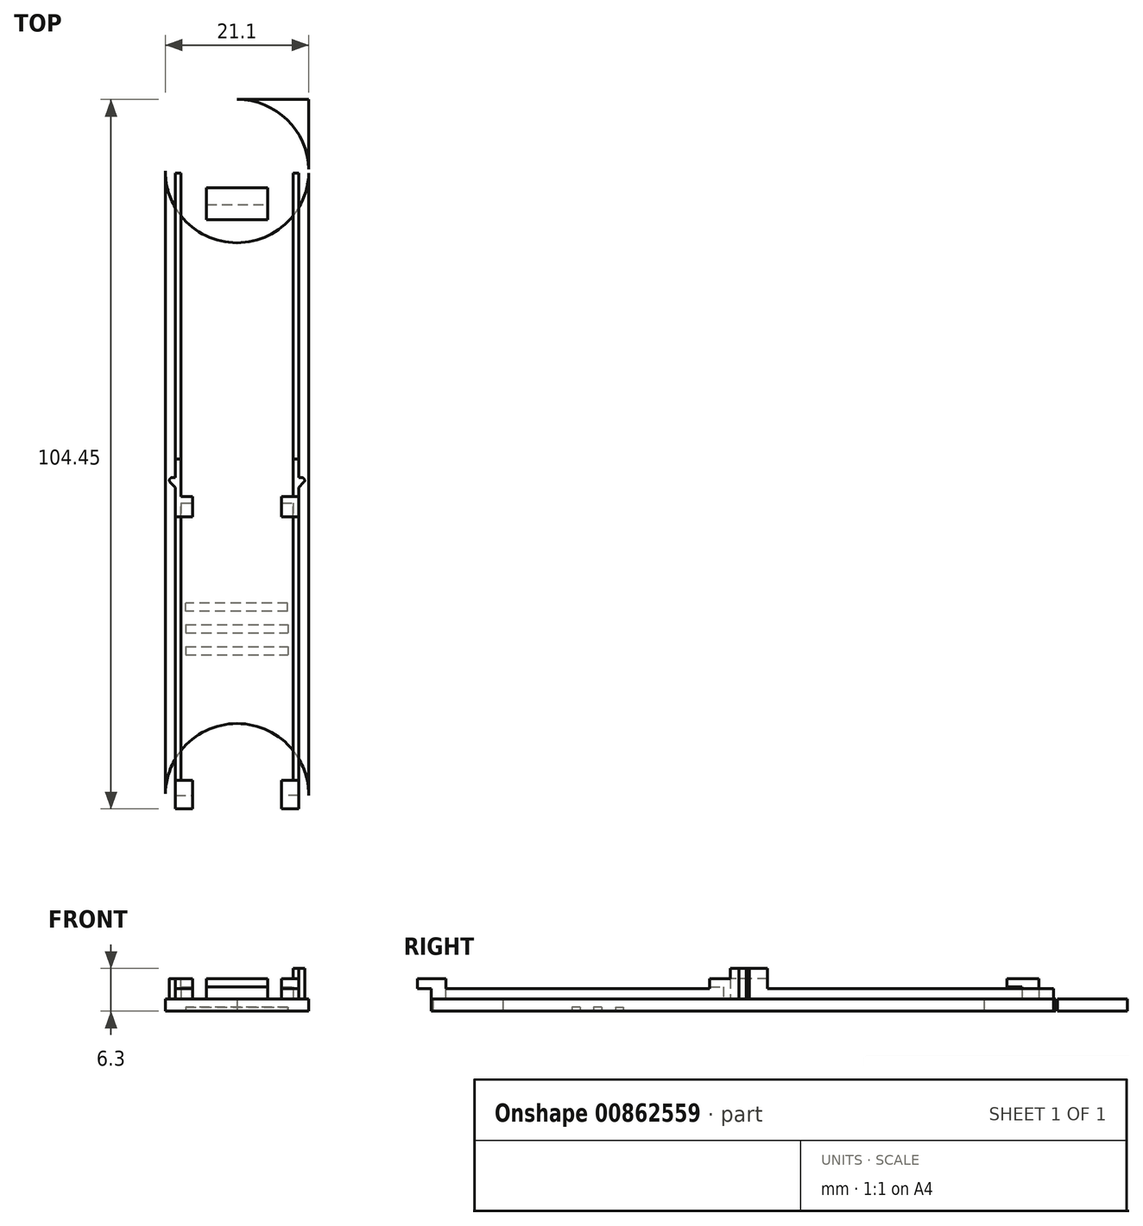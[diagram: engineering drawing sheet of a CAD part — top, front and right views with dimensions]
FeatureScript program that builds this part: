
annotation { "Feature Type Name" : "Feature", "Feature Type Description" : "" }
export const myFeature = defineFeature(function(context is Context, id is Id, definition is map)
    precondition{}
    {
        {
            var Q0;
            Q0=qCreatedBy(makeId("Top.planeOp"),FACE);
            var sketch = newSketch(context, id + "F0", { "sketchPlane" : qUnion([Q0])});
            skLineSegment(sketch, "E0.bottom", {"start": v(10.55, -56.5) * mm, "end": v(-10.55, -56.5) * mm});
            skLineSegment(sketch, "E0.top", {"start": v(10.55, 56.5) * mm, "end": v(-10.55, 56.5) * mm});
            skLineSegment(sketch, "E0.left", {"start": v(10.55, -56.5) * mm, "end": v(10.55, 56.5) * mm});
            skLineSegment(sketch, "E0.right", {"start": v(-10.55, -56.5) * mm, "end": v(-10.55, 56.5) * mm});
            skPoint(sketch, "E0.middle", {"position": v(0, 0) * mm});
            skCircle(sketch, "E1", {"center": v(0, 45.95) * mm, "radius": 10.55 * mm});
            skPoint(sketch, "E1.first.point", {"position": v(-10.55, 45.95) * mm});
            skPoint(sketch, "E1.second.point", {"position": v(0, 56.5) * mm});
            skPoint(sketch, "E1.third.point", {"position": v(10.55, 45.66) * mm});
            skCircle(sketch, "E2", {"center": v(0, -45.95) * mm, "radius": 10.55 * mm});
            skPoint(sketch, "E2.first.point", {"position": v(0, -35.4) * mm});
            skPoint(sketch, "E2.second.point", {"position": v(0, -56.5) * mm});
            skPoint(sketch, "E2.third.point", {"position": v(-10.55, -46.2) * mm});
            skSolve(sketch);
        }
        {
            var Q0;
            {var subQ0=sQuery(id+"F0.wireOp",EDGE,"E1");var subQ1=sQuery(id+"F0.wireOp",EDGE,"E0.left");var subQ2=makeQuery(id+"F0.imprint","INTERSECT",VERTEX,{"disambiguationData":[OD(0.0)],"derivedFrom":[subQ1,subQ0]});Q0=makeQuery(id+"F0.imprint","IMPRINT",FACE,{"disambiguationData":[TD([[makeQuery(id+"F0.imprint","IMPRINT",EDGE,{"disambiguationData":[TD([[subQ2,-1.0]])],"derivedFrom":subQ1}),-1.0]])]});}
            var Q1;
            {var subQ0=sQuery(id+"F0.wireOp",EDGE,"E2");var subQ1=sQuery(id+"F0.wireOp",EDGE,"E0.right");var subQ2=makeQuery(id+"F0.imprint","INTERSECT",VERTEX,{"disambiguationData":[OD(0.0)],"derivedFrom":[subQ1,subQ0]});Q1=makeQuery(id+"F0.imprint","IMPRINT",FACE,{"disambiguationData":[TD([[makeQuery(id+"F0.imprint","IMPRINT",EDGE,{"disambiguationData":[TD([[subQ2,-1.0]])],"derivedFrom":subQ1}),1.0]])]});}
            var Q2;
            {var subQ0=sQuery(id+"F0.wireOp",EDGE,"E2");var subQ1=sQuery(id+"F0.wireOp",EDGE,"E0.left");var subQ2=makeQuery(id+"F0.imprint","INTERSECT",VERTEX,{"derivedFrom":[subQ1,subQ0]});Q2=makeQuery(id+"F0.imprint","IMPRINT",FACE,{"disambiguationData":[TD([[makeQuery(id+"F0.imprint","IMPRINT",EDGE,{"disambiguationData":[TD([[subQ2,-1.0]])],"derivedFrom":subQ1}),1.0]])]});}
            var Q3;
            {var subQ0=sQuery(id+"F0.wireOp",EDGE,"E2");var subQ1=sQuery(id+"F0.wireOp",EDGE,"E0.right");var subQ2=makeQuery(id+"F0.imprint","INTERSECT",VERTEX,{"disambiguationData":[OD(0.0)],"derivedFrom":[subQ1,subQ0]});Q3=makeQuery(id+"F0.imprint","IMPRINT",FACE,{"disambiguationData":[TD([[makeQuery(id+"F0.imprint","IMPRINT",EDGE,{"disambiguationData":[TD([[subQ2,-1.0]])],"derivedFrom":subQ1}),-1.0]])]});}
            var Q4;
            {var subQ0=sQuery(id+"F0.wireOp",EDGE,"E1");var subQ1=sQuery(id+"F0.wireOp",EDGE,"E0.left");var subQ2=makeQuery(id+"F0.imprint","INTERSECT",VERTEX,{"disambiguationData":[OD(0.0)],"derivedFrom":[subQ1,subQ0]});Q4=makeQuery(id+"F0.imprint","IMPRINT",FACE,{"disambiguationData":[TD([[makeQuery(id+"F0.imprint","IMPRINT",EDGE,{"disambiguationData":[TD([[subQ2,-1.0]])],"derivedFrom":subQ1}),1.0]])]});}
            extrude(context, id + "F1", {"entities" : qUnion([Q0, Q1, Q2, Q3, Q4]), "depth" : 1.8 * mm, "offsetDistance" : 25.4 * mm});
        }
        {
            var Q0;
            Q0=makeQuery(id+"F1.opExtrude","CAP_FACE",FACE,{"disambiguationData":[OSD([sQuery(id+"F0.wireOp",EDGE,"E0.left"),sQuery(id+"F0.wireOp",EDGE,"E0.right"),sQuery(id+"F0.wireOp",EDGE,"E1"),sQuery(id+"F0.wireOp",EDGE,"E2")])],"isStart":true});
            var sketch = newSketch(context, id + "F2", { "sketchPlane" : qUnion([Q0])});
            skLineSegment(sketch, "E3", {"start": v(0, -45.95) * mm, "end": v(0, -45.95) * mm});
            skLineSegment(sketch, "E4", {"start": v(0, -45.95) * mm, "end": v(-2.54, -45.95) * mm});
            skLineSegment(sketch, "E5", {"start": v(-2.54, -45.95) * mm, "end": v(0, -50.24) * mm});
            skLineSegment(sketch, "E6", {"start": v(0, -50.24) * mm, "end": v(2.66, -45.95) * mm});
            skLineSegment(sketch, "E7", {"start": v(2.66, -45.95) * mm, "end": v(0, -45.95) * mm});
            skLineSegment(sketch, "E8.bottom", {"start": v(7.45, 18.85) * mm, "end": v(-7.55, 18.85) * mm});
            skLineSegment(sketch, "E8.top", {"start": v(7.45, 17.65) * mm, "end": v(-7.55, 17.65) * mm});
            skLineSegment(sketch, "E8.left", {"start": v(7.45, 18.85) * mm, "end": v(7.45, 17.65) * mm});
            skLineSegment(sketch, "E8.right", {"start": v(-7.55, 18.85) * mm, "end": v(-7.55, 17.65) * mm});
            skLineSegment(sketch, "E9.bottom", {"start": v(-7.55, 20.85) * mm, "end": v(7.46, 20.85) * mm});
            skLineSegment(sketch, "E9.left", {"start": v(-7.55, 20.85) * mm, "end": v(-7.55, 22.05) * mm});
            skLineSegment(sketch, "E9.right", {"start": v(7.46, 20.85) * mm, "end": v(7.46, 22.05) * mm});
            skLineSegment(sketch, "E10", {"start": v(-7.55, 22.05) * mm, "end": v(7.46, 22.05) * mm});
            skLineSegment(sketch, "E11.bottom", {"start": v(-7.55, 24.05) * mm, "end": v(7.46, 24.05) * mm});
            skLineSegment(sketch, "E11.top", {"start": v(-7.55, 25.25) * mm, "end": v(7.46, 25.25) * mm});
            skLineSegment(sketch, "E11.left", {"start": v(-7.55, 24.05) * mm, "end": v(-7.55, 25.25) * mm});
            skLineSegment(sketch, "E11.right", {"start": v(7.46, 24.05) * mm, "end": v(7.46, 25.25) * mm});
            skLineSegment(sketch, "E12", {"start": v(10.55, 0) * mm, "end": v(-10.55, -0.12) * mm, "construction": true});
            skSolve(sketch);
        }
        {
            var Q0;
            Q0=makeQuery(id+"F2.imprint","IMPRINT",FACE,{"disambiguationData":[TD([[makeQuery(id+"F2.imprint","IMPRINT",EDGE,{"derivedFrom":sQuery(id+"F2.wireOp",EDGE,"E4")}),1.0]])]});
            var Q1;
            Q1=makeQuery(id+"F2.imprint","IMPRINT",FACE,{"disambiguationData":[TD([[makeQuery(id+"F2.imprint","IMPRINT",EDGE,{"derivedFrom":sQuery(id+"F2.wireOp",EDGE,"E8.bottom")}),1.0]])]});
            var Q2;
            Q2=makeQuery(id+"F2.imprint","IMPRINT",FACE,{"disambiguationData":[TD([[makeQuery(id+"F2.imprint","IMPRINT",EDGE,{"derivedFrom":sQuery(id+"F2.wireOp",EDGE,"E9.bottom")}),1.0]])]});
            var Q3;
            Q3=makeQuery(id+"F2.imprint","IMPRINT",FACE,{"disambiguationData":[TD([[makeQuery(id+"F2.imprint","IMPRINT",EDGE,{"derivedFrom":sQuery(id+"F2.wireOp",EDGE,"E11.bottom")}),1.0]])]});
            extrude(context, id + "F3", {"entities" : qUnion([Q0, Q1, Q2, Q3]), "operationType" : NewBodyOperationType.REMOVE, "oppositeDirection" : true, "depth" : .6 * mm, "offsetDistance" : 25.4 * mm});
        }
        {
            var Q0;
            Q0=makeQuery(id+"F2.imprint","IMPRINT",FACE,{"disambiguationData":[TD([[makeQuery(id+"F2.imprint","IMPRINT",EDGE,{"derivedFrom":sQuery(id+"F2.wireOp",EDGE,"E8.bottom")}),1.0]])]});
            var Q1;
            Q1=makeQuery(id+"F2.imprint","IMPRINT",FACE,{"disambiguationData":[TD([[makeQuery(id+"F2.imprint","IMPRINT",EDGE,{"derivedFrom":sQuery(id+"F2.wireOp",EDGE,"E9.bottom")}),1.0]])]});
            var Q2;
            Q2=makeQuery(id+"F2.imprint","IMPRINT",FACE,{"disambiguationData":[TD([[makeQuery(id+"F2.imprint","IMPRINT",EDGE,{"derivedFrom":sQuery(id+"F2.wireOp",EDGE,"E11.bottom")}),1.0]])]});
            var Q3;
            Q3=sQuery(id+"F2.wireOp",EDGE,"E8.bottom");
            extrude(context, id + "F4", {"entities" : qUnion([Q0, Q1, Q2]), "operationType" : NewBodyOperationType.REMOVE, "surfaceEntities" : qUnion([Q3]), "oppositeDirection" : true, "depth" : .35 * mm, "offsetDistance" : 25.4 * mm});
        }
        {
            var Q0;
            Q0=makeQuery(id+"F1.opExtrude","CAP_FACE",FACE,{"disambiguationData":[OSD([sQuery(id+"F0.wireOp",EDGE,"E0.left"),sQuery(id+"F0.wireOp",EDGE,"E0.right"),sQuery(id+"F0.wireOp",EDGE,"E1"),sQuery(id+"F0.wireOp",EDGE,"E2")])],"isStart":false});
            var sketch = newSketch(context, id + "F5", { "sketchPlane" : qUnion([Q0])});
            skLineSegment(sketch, "E13.bottom", {"start": v(4.5, 43.5) * mm, "end": v(-4.5, 43.5) * mm});
            skLineSegment(sketch, "E13.top", {"start": v(4.5, 41) * mm, "end": v(-4.5, 41) * mm});
            skLineSegment(sketch, "E13.left", {"start": v(4.5, 43.5) * mm, "end": v(4.5, 41) * mm});
            skLineSegment(sketch, "E13.right", {"start": v(-4.5, 43.5) * mm, "end": v(-4.5, 41) * mm});
            skLineSegment(sketch, "E14.bottom", {"start": v(8.25, 45.66) * mm, "end": v(9.05, 45.66) * mm});
            skLineSegment(sketch, "E14.top", {"start": v(8.25, -45.95) * mm, "end": v(9.05, -45.95) * mm});
            skLineSegment(sketch, "E14.left", {"start": v(8.25, 45.66) * mm, "end": v(8.25, -45.95) * mm});
            skLineSegment(sketch, "E14.right", {"start": v(9.05, 45.66) * mm, "end": v(9.05, -45.95) * mm});
            skLineSegment(sketch, "E15.bottom", {"start": v(-9.07, 45.66) * mm, "end": v(-8.27, 45.66) * mm});
            skLineSegment(sketch, "E15.top", {"start": v(-9.07, -45.95) * mm, "end": v(-8.27, -45.95) * mm});
            skLineSegment(sketch, "E15.left", {"start": v(-9.07, 45.66) * mm, "end": v(-9.07, -45.95) * mm});
            skLineSegment(sketch, "E15.right", {"start": v(-8.27, 45.66) * mm, "end": v(-8.27, -45.95) * mm});
            skLineSegment(sketch, "E16.bottom", {"start": v(9.05, -45.95) * mm, "end": v(6.55, -45.95) * mm});
            skLineSegment(sketch, "E16.top", {"start": v(9.05, -43.75) * mm, "end": v(6.55, -43.75) * mm});
            skLineSegment(sketch, "E16.left", {"start": v(9.05, -45.95) * mm, "end": v(9.05, -43.75) * mm});
            skLineSegment(sketch, "E16.right", {"start": v(6.55, -45.95) * mm, "end": v(6.55, -43.75) * mm});
            skPoint(sketch, "E17.oppositeSnap0", {"position": v(7.8, -45.95) * mm});
            skLineSegment(sketch, "E17.bottom", {"start": v(-9.07, -43.75) * mm, "end": v(-6.57, -43.75) * mm});
            skLineSegment(sketch, "E17.top", {"start": v(-9.07, -45.95) * mm, "end": v(-6.57, -45.95) * mm});
            skLineSegment(sketch, "E17.left", {"start": v(-9.07, -43.75) * mm, "end": v(-9.07, -45.95) * mm});
            skLineSegment(sketch, "E17.right", {"start": v(-6.57, -43.75) * mm, "end": v(-6.57, -45.95) * mm});
            skLineSegment(sketch, "E18.bottom", {"start": v(6.55, -1.95) * mm, "end": v(9.05, -1.95) * mm});
            skLineSegment(sketch, "E18.top", {"start": v(6.55, -2.95) * mm, "end": v(9.05, -2.95) * mm});
            skLineSegment(sketch, "E18.left", {"start": v(6.55, -1.95) * mm, "end": v(6.55, -2.95) * mm});
            skLineSegment(sketch, "E18.right", {"start": v(9.05, -1.95) * mm, "end": v(9.05, -2.95) * mm});
            skPoint(sketch, "E19.firstSnap0", {"position": v(7.8, -1.95) * mm});
            skLineSegment(sketch, "E19.bottom", {"start": v(-9.07, -1.95) * mm, "end": v(-6.57, -1.95) * mm});
            skLineSegment(sketch, "E19.top", {"start": v(-9.07, -2.95) * mm, "end": v(-6.57, -2.95) * mm});
            skLineSegment(sketch, "E19.left", {"start": v(-9.07, -1.95) * mm, "end": v(-9.07, -2.95) * mm});
            skLineSegment(sketch, "E19.right", {"start": v(-6.57, -1.95) * mm, "end": v(-6.57, -2.95) * mm});
            skLineSegment(sketch, "E20.bottom", {"start": v(-9.07, -1.95) * mm, "end": v(-8.27, -1.95) * mm});
            skLineSegment(sketch, "E20.top", {"start": v(-9.07, 3.55) * mm, "end": v(-8.27, 3.55) * mm});
            skLineSegment(sketch, "E20.left", {"start": v(-9.07, -1.95) * mm, "end": v(-9.07, 3.55) * mm});
            skLineSegment(sketch, "E20.right", {"start": v(-8.27, -1.95) * mm, "end": v(-8.27, 3.55) * mm});
            skLineSegment(sketch, "E21.bottom", {"start": v(9.05, 3.55) * mm, "end": v(8.25, 3.55) * mm});
            skLineSegment(sketch, "E21.top", {"start": v(9.05, -1.95) * mm, "end": v(8.25, -1.95) * mm});
            skLineSegment(sketch, "E21.left", {"start": v(9.05, 3.55) * mm, "end": v(9.05, -1.95) * mm});
            skLineSegment(sketch, "E21.right", {"start": v(8.25, 3.55) * mm, "end": v(8.25, -1.95) * mm});
            skSolve(sketch);
        }
        {
            var Q0;
            Q0 = qSketchRegion(id + "F5", true);
            extrude(context, id + "F6", {"entities" : qUnion([Q0]), "operationType" : NewBodyOperationType.ADD, "depth" : 3 * mm, "offsetDistance" : 25.4 * mm});
        }
        {
            var Q0;
            Q0=makeQuery(id+"F5.imprint","IMPRINT",FACE,{"disambiguationData":[TD([[makeQuery(id+"F5.imprint","IMPRINT",EDGE,{"derivedFrom":sQuery(id+"F5.wireOp",EDGE,"E20.bottom")}),1.0]])]});
            var Q1;
            Q1=makeQuery(id+"F5.imprint","IMPRINT",FACE,{"disambiguationData":[TD([[makeQuery(id+"F5.imprint","IMPRINT",EDGE,{"derivedFrom":sQuery(id+"F5.wireOp",EDGE,"E21.bottom")}),1.0]])]});
            extrude(context, id + "F7", {"entities" : qUnion([Q0, Q1]), "operationType" : NewBodyOperationType.ADD, "depth" : 4.5 * mm, "offsetDistance" : 25.4 * mm});
        }
        {
            var Q0;
            Q0=makeQuery(id+"F6.opExtrude","SWEPT_FACE",FACE,{"disambiguationData":[OSD([sQuery(id+"F5.wireOp",EDGE,"E13.top")])]});
            var sketch = newSketch(context, id + "F8", { "sketchPlane" : qUnion([Q0])});
            skLineSegment(sketch, "E22.bottom", {"start": v(-4.5, 4.8) * mm, "end": v(4.5, 4.8) * mm});
            skLineSegment(sketch, "E22.top", {"start": v(-4.5, 3.6) * mm, "end": v(4.5, 3.6) * mm});
            skLineSegment(sketch, "E22.left", {"start": v(-4.5, 4.8) * mm, "end": v(-4.5, 3.6) * mm});
            skLineSegment(sketch, "E22.right", {"start": v(4.5, 4.8) * mm, "end": v(4.5, 3.6) * mm});
            skSolve(sketch);
        }
        {
            var Q0;
            Q0 = qSketchRegion(id + "F8", true);
            extrude(context, id + "F9", {"entities" : qUnion([Q0]), "operationType" : NewBodyOperationType.ADD, "depth" : 2.2 * mm, "offsetDistance" : 25.4 * mm});
        }
        {
            var Q0;
            Q0=makeQuery(id+"F6.opExtrude","SWEPT_FACE",FACE,{"disambiguationData":[OSD([sQuery(id+"F5.wireOp",EDGE,"E19.top")])]});
            var sketch = newSketch(context, id + "F10", { "sketchPlane" : qUnion([Q0])});
            skLineSegment(sketch, "E23.bottom", {"start": v(-8.27, 4.8) * mm, "end": v(-6.57, 4.8) * mm});
            skLineSegment(sketch, "E23.top", {"start": v(-8.27, 3.6) * mm, "end": v(-6.57, 3.6) * mm});
            skLineSegment(sketch, "E23.left", {"start": v(-8.27, 4.8) * mm, "end": v(-8.27, 3.6) * mm});
            skLineSegment(sketch, "E23.right", {"start": v(-6.57, 4.8) * mm, "end": v(-6.57, 3.6) * mm});
            skSolve(sketch);
        }
        {
            var Q0;
            Q0=makeQuery(id+"F6.opExtrude","SWEPT_FACE",FACE,{"disambiguationData":[OSD([sQuery(id+"F5.wireOp",EDGE,"E18.top")])]});
            var sketch = newSketch(context, id + "F11", { "sketchPlane" : qUnion([Q0])});
            skLineSegment(sketch, "E24.bottom", {"start": v(6.55, 4.8) * mm, "end": v(8.25, 4.8) * mm});
            skLineSegment(sketch, "E24.top", {"start": v(6.55, 3.6) * mm, "end": v(8.25, 3.6) * mm});
            skLineSegment(sketch, "E24.left", {"start": v(6.55, 4.8) * mm, "end": v(6.55, 3.6) * mm});
            skLineSegment(sketch, "E24.right", {"start": v(8.25, 4.8) * mm, "end": v(8.25, 3.6) * mm});
            skSolve(sketch);
        }
        {
            var Q0;
            Q0=makeQuery(id+"F6.opExtrude","SWEPT_FACE",FACE,{"disambiguationData":[OSD([sQuery(id+"F5.wireOp",EDGE,"E17.top")])]});
            var sketch = newSketch(context, id + "F12", { "sketchPlane" : qUnion([Q0])});
            skLineSegment(sketch, "E25.bottom", {"start": v(-9.07, 4.8) * mm, "end": v(-6.57, 4.8) * mm});
            skLineSegment(sketch, "E25.top", {"start": v(-9.07, 3.3) * mm, "end": v(-6.57, 3.3) * mm});
            skLineSegment(sketch, "E25.left", {"start": v(-9.07, 4.8) * mm, "end": v(-9.07, 3.3) * mm});
            skLineSegment(sketch, "E25.right", {"start": v(-6.57, 4.8) * mm, "end": v(-6.57, 3.3) * mm});
            skSolve(sketch);
        }
        {
            var Q0;
            Q0=makeQuery(id+"F6.opExtrude","SWEPT_FACE",FACE,{"disambiguationData":[OSD([sQuery(id+"F5.wireOp",EDGE,"E16.bottom")])]});
            var sketch = newSketch(context, id + "F13", { "sketchPlane" : qUnion([Q0])});
            skLineSegment(sketch, "E26.bottom", {"start": v(6.55, 4.8) * mm, "end": v(9.05, 4.8) * mm});
            skLineSegment(sketch, "E26.top", {"start": v(6.55, 3.3) * mm, "end": v(9.05, 3.3) * mm});
            skLineSegment(sketch, "E26.left", {"start": v(6.55, 4.8) * mm, "end": v(6.55, 3.3) * mm});
            skLineSegment(sketch, "E26.right", {"start": v(9.05, 4.8) * mm, "end": v(9.05, 3.3) * mm});
            skSolve(sketch);
        }
        {
            var Q0;
            Q0 = qSketchRegion(id + "F10", true);
            var Q1;
            Q1=makeQuery(id+"F11.imprint","IMPRINT",FACE,{"disambiguationData":[TD([[makeQuery(id+"F11.imprint","IMPRINT",EDGE,{"derivedFrom":sQuery(id+"F11.wireOp",EDGE,"E24.bottom")}),-1.0]])]});
            var Q2;
            Q2=makeQuery(id+"F13.imprint","IMPRINT",FACE,{"disambiguationData":[TD([[makeQuery(id+"F13.imprint","IMPRINT",EDGE,{"derivedFrom":sQuery(id+"F13.wireOp",EDGE,"E26.bottom")}),1.0]])]});
            var Q3;
            Q3=makeQuery(id+"F12.imprint","IMPRINT",FACE,{"disambiguationData":[TD([[makeQuery(id+"F12.imprint","IMPRINT",EDGE,{"derivedFrom":sQuery(id+"F12.wireOp",EDGE,"E25.bottom")}),-1.0]])]});
            extrude(context, id + "F14", {"entities" : qUnion([Q0, Q1, Q2, Q3]), "operationType" : NewBodyOperationType.ADD, "depth" : 2 * mm, "offsetDistance" : 25.4 * mm});
        }
        {
            var Q0;
            {var subQ0=sQuery(id+"F5.wireOp",EDGE,"E18.left");var subQ1=sQuery(id+"F5.wireOp",EDGE,"E18.top");var subQ2=sQuery(id+"F5.wireOp",EDGE,"E18.bottom");var subQ3=sQuery(id+"F5.wireOp",EDGE,"E16.top");var subQ4=sQuery(id+"F5.wireOp",EDGE,"E16.right");var subQ5=sQuery(id+"F5.wireOp",EDGE,"E21.right");var subQ6=sQuery(id+"F5.wireOp",EDGE,"E14.left");var subQ7=sQuery(id+"F5.wireOp",EDGE,"E21.left");var subQ8=sQuery(id+"F5.wireOp",EDGE,"E18.right");var subQ9=sQuery(id+"F5.wireOp",EDGE,"E16.left");var subQ10=sQuery(id+"F5.wireOp",EDGE,"E14.right");var subQ11=sQuery(id+"F5.wireOp",EDGE,"E16.bottom");Q0=makeQuery(id+"F14.boolean.opBoolean","MERGE",FACE,{"derivedFrom":[makeQuery(id+"F7.boolean.opBoolean","SPLIT",FACE,{"disambiguationData":[TD([makeQuery(id+"F6.opExtrude","SWEPT_FACE",FACE,{"disambiguationData":[OSD([subQ6])]})])],"derivedFrom":makeQuery(id+"F6.opExtrude","CAP_FACE",FACE,{"disambiguationData":[OSD([sQuery(id+"F5.wireOp",EDGE,"E14.bottom"),subQ6,subQ10,subQ11,subQ3,subQ9,subQ4,subQ2,subQ1,subQ0,subQ8,subQ7,subQ5])],"isStart":false})}),makeQuery(id+"F14.opExtrude","SWEPT_FACE",FACE,{"disambiguationData":[OSD([sQuery(id+"F11.wireOp",EDGE,"E24.bottom")])]}),makeQuery(id+"F14.opExtrude","SWEPT_FACE",FACE,{"disambiguationData":[OSD([sQuery(id+"F13.wireOp",EDGE,"E26.bottom")])]})]});}
            var sketch = newSketch(context, id + "F15", { "sketchPlane" : qUnion([Q0])});
            skLineSegment(sketch, "E27.bottom", {"start": v(8.25, -4.95) * mm, "end": v(9.05, -4.95) * mm});
            skLineSegment(sketch, "E27.top", {"start": v(8.25, -43.75) * mm, "end": v(9.05, -43.75) * mm});
            skLineSegment(sketch, "E27.left", {"start": v(8.25, -4.95) * mm, "end": v(8.25, -43.75) * mm});
            skLineSegment(sketch, "E27.right", {"start": v(9.05, -4.95) * mm, "end": v(9.05, -43.75) * mm});
            skSolve(sketch);
        }
        {
            var Q0;
            {var subQ0=sQuery(id+"F5.wireOp",EDGE,"E19.right");var subQ1=sQuery(id+"F5.wireOp",EDGE,"E17.right");var subQ2=sQuery(id+"F5.wireOp",EDGE,"E20.right");var subQ3=sQuery(id+"F5.wireOp",EDGE,"E17.top");var subQ4=sQuery(id+"F5.wireOp",EDGE,"E20.left");var subQ5=sQuery(id+"F5.wireOp",EDGE,"E19.left");var subQ6=sQuery(id+"F5.wireOp",EDGE,"E17.left");var subQ7=sQuery(id+"F5.wireOp",EDGE,"E15.left");var subQ8=sQuery(id+"F5.wireOp",EDGE,"E19.bottom");var subQ9=sQuery(id+"F5.wireOp",EDGE,"E15.right");var subQ10=sQuery(id+"F5.wireOp",EDGE,"E17.bottom");var subQ11=sQuery(id+"F5.wireOp",EDGE,"E19.top");Q0=makeQuery(id+"F14.boolean.opBoolean","MERGE",FACE,{"derivedFrom":[makeQuery(id+"F7.boolean.opBoolean","SPLIT",FACE,{"disambiguationData":[TD([makeQuery(id+"F6.opExtrude","SWEPT_FACE",FACE,{"disambiguationData":[OSD([subQ9])]})])],"derivedFrom":makeQuery(id+"F6.opExtrude","CAP_FACE",FACE,{"disambiguationData":[OSD([sQuery(id+"F5.wireOp",EDGE,"E15.bottom"),subQ7,subQ9,subQ10,subQ3,subQ6,subQ1,subQ8,subQ11,subQ5,subQ0,subQ4,subQ2])],"isStart":false})}),makeQuery(id+"F14.opExtrude","SWEPT_FACE",FACE,{"disambiguationData":[OSD([sQuery(id+"F10.wireOp",EDGE,"E23.bottom")])]}),makeQuery(id+"F14.opExtrude","SWEPT_FACE",FACE,{"disambiguationData":[OSD([sQuery(id+"F12.wireOp",EDGE,"E25.bottom")])]})]});}
            var sketch = newSketch(context, id + "F16", { "sketchPlane" : qUnion([Q0])});
            skLineSegment(sketch, "E28.bottom", {"start": v(-8.27, -4.95) * mm, "end": v(-9.07, -4.95) * mm});
            skLineSegment(sketch, "E28.top", {"start": v(-8.27, -43.75) * mm, "end": v(-9.07, -43.75) * mm});
            skLineSegment(sketch, "E28.left", {"start": v(-8.27, -4.95) * mm, "end": v(-8.27, -43.75) * mm});
            skLineSegment(sketch, "E28.right", {"start": v(-9.07, -4.95) * mm, "end": v(-9.07, -43.75) * mm});
            skSolve(sketch);
        }
        {
            var Q0;
            {var subQ0=sQuery(id+"F5.wireOp",EDGE,"E20.right");var subQ1=sQuery(id+"F5.wireOp",EDGE,"E15.right");var subQ2=sQuery(id+"F5.wireOp",EDGE,"E20.left");var subQ3=sQuery(id+"F5.wireOp",EDGE,"E19.left");var subQ4=sQuery(id+"F5.wireOp",EDGE,"E17.left");var subQ5=sQuery(id+"F5.wireOp",EDGE,"E15.left");var subQ6=sQuery(id+"F5.wireOp",EDGE,"E15.bottom");Q0=makeQuery(id+"F7.boolean.opBoolean","SPLIT",FACE,{"disambiguationData":[TD([makeQuery(id+"F6.opExtrude","SWEPT_FACE",FACE,{"disambiguationData":[OSD([subQ6])]})])],"derivedFrom":makeQuery(id+"F6.opExtrude","CAP_FACE",FACE,{"disambiguationData":[OSD([subQ6,subQ5,subQ1,sQuery(id+"F5.wireOp",EDGE,"E17.bottom"),sQuery(id+"F5.wireOp",EDGE,"E17.top"),subQ4,sQuery(id+"F5.wireOp",EDGE,"E17.right"),sQuery(id+"F5.wireOp",EDGE,"E19.bottom"),sQuery(id+"F5.wireOp",EDGE,"E19.top"),subQ3,sQuery(id+"F5.wireOp",EDGE,"E19.right"),subQ2,subQ0])],"isStart":false})});}
            var sketch = newSketch(context, id + "F17", { "sketchPlane" : qUnion([Q0])});
            skLineSegment(sketch, "E29.bottom", {"start": v(-9.07, 45.66) * mm, "end": v(-8.27, 45.66) * mm});
            skLineSegment(sketch, "E29.top", {"start": v(-9.07, 3.55) * mm, "end": v(-8.27, 3.55) * mm});
            skLineSegment(sketch, "E29.left", {"start": v(-9.07, 45.66) * mm, "end": v(-9.07, 3.55) * mm});
            skLineSegment(sketch, "E29.right", {"start": v(-8.27, 45.66) * mm, "end": v(-8.27, 3.55) * mm});
            skSolve(sketch);
        }
        {
            var Q0;
            {var subQ0=sQuery(id+"F5.wireOp",EDGE,"E21.right");var subQ1=sQuery(id+"F5.wireOp",EDGE,"E14.left");var subQ2=sQuery(id+"F5.wireOp",EDGE,"E21.left");var subQ3=sQuery(id+"F5.wireOp",EDGE,"E18.right");var subQ4=sQuery(id+"F5.wireOp",EDGE,"E16.left");var subQ5=sQuery(id+"F5.wireOp",EDGE,"E14.right");var subQ6=sQuery(id+"F5.wireOp",EDGE,"E14.bottom");Q0=makeQuery(id+"F7.boolean.opBoolean","SPLIT",FACE,{"disambiguationData":[TD([makeQuery(id+"F6.opExtrude","SWEPT_FACE",FACE,{"disambiguationData":[OSD([subQ6])]})])],"derivedFrom":makeQuery(id+"F6.opExtrude","CAP_FACE",FACE,{"disambiguationData":[OSD([subQ6,subQ1,subQ5,sQuery(id+"F5.wireOp",EDGE,"E16.bottom"),sQuery(id+"F5.wireOp",EDGE,"E16.top"),subQ4,sQuery(id+"F5.wireOp",EDGE,"E16.right"),sQuery(id+"F5.wireOp",EDGE,"E18.bottom"),sQuery(id+"F5.wireOp",EDGE,"E18.top"),sQuery(id+"F5.wireOp",EDGE,"E18.left"),subQ3,subQ2,subQ0])],"isStart":false})});}
            var sketch = newSketch(context, id + "F18", { "sketchPlane" : qUnion([Q0])});
            skLineSegment(sketch, "E30.bottom", {"start": v(8.25, 45.66) * mm, "end": v(9.05, 45.66) * mm});
            skLineSegment(sketch, "E30.top", {"start": v(8.25, 3.55) * mm, "end": v(9.05, 3.55) * mm});
            skLineSegment(sketch, "E30.left", {"start": v(8.25, 45.66) * mm, "end": v(8.25, 3.55) * mm});
            skLineSegment(sketch, "E30.right", {"start": v(9.05, 45.66) * mm, "end": v(9.05, 3.55) * mm});
            skSolve(sketch);
        }
        {
            var Q0;
            Q0=makeQuery(id+"F17.imprint","IMPRINT",FACE,{"disambiguationData":[TD([[makeQuery(id+"F17.imprint","IMPRINT",EDGE,{"derivedFrom":sQuery(id+"F17.wireOp",EDGE,"E29.bottom")}),-1.0]])]});
            var Q1;
            Q1=makeQuery(id+"F18.imprint","IMPRINT",FACE,{"disambiguationData":[TD([[makeQuery(id+"F18.imprint","IMPRINT",EDGE,{"derivedFrom":sQuery(id+"F18.wireOp",EDGE,"E30.bottom")}),-1.0]])]});
            var Q2;
            Q2=makeQuery(id+"F15.imprint","IMPRINT",FACE,{"disambiguationData":[TD([[makeQuery(id+"F15.imprint","IMPRINT",EDGE,{"derivedFrom":sQuery(id+"F15.wireOp",EDGE,"E27.bottom")}),-1.0]])]});
            var Q3;
            {var subQ3=sQuery(id+"F16.wireOp",EDGE,"E28.bottom");Q3=makeQuery(id+"F16.imprint","IMPRINT",FACE,{"disambiguationData":[TD([[makeQuery(id+"F16.imprint","IMPRINT",EDGE,{"derivedFrom":subQ3}),1.0]])]});}
            extrude(context, id + "F19", {"entities" : qUnion([Q0, Q1, Q2, Q3]), "operationType" : NewBodyOperationType.REMOVE, "oppositeDirection" : true, "depth" : 1.5 * mm, "offsetDistance" : 25.4 * mm});
        }
        {
            var Q0;
            {var subQ0=sQuery(id+"F5.wireOp",EDGE,"E21.left");Q0=makeQuery(id+"F14.boolean.opBoolean","MERGE",FACE,{"derivedFrom":[makeQuery(id+"F7.boolean.opBoolean","MERGE",FACE,{"derivedFrom":[makeQuery(id+"F6.opExtrude","SWEPT_FACE",FACE,{"disambiguationData":[OSD([sQuery(id+"F5.wireOp",EDGE,"E14.right"),sQuery(id+"F5.wireOp",EDGE,"E16.left"),sQuery(id+"F5.wireOp",EDGE,"E18.right"),subQ0])]}),makeQuery(id+"F7.opExtrude","SWEPT_FACE",FACE,{"disambiguationData":[OSD([subQ0])]})]}),makeQuery(id+"F14.opExtrude","SWEPT_FACE",FACE,{"disambiguationData":[OSD([sQuery(id+"F13.wireOp",EDGE,"E26.right")])]})]});}
            var sketch = newSketch(context, id + "F20", { "sketchPlane" : qUnion([Q0])});
            skLineSegment(sketch, "E31.bottom", {"start": v(-0.65, 6.3) * mm, "end": v(0.85, 6.3) * mm});
            skLineSegment(sketch, "E31.top", {"start": v(-0.65, 1.8) * mm, "end": v(0.85, 1.8) * mm});
            skLineSegment(sketch, "E31.left", {"start": v(-0.65, 6.3) * mm, "end": v(-0.65, 1.8) * mm});
            skLineSegment(sketch, "E31.right", {"start": v(0.85, 6.3) * mm, "end": v(0.85, 1.8) * mm});
            skSolve(sketch);
        }
        {
            var Q0;
            Q0 = qSketchRegion(id + "F20", true);
            extrude(context, id + "F21", {"entities" : qUnion([Q0]), "operationType" : NewBodyOperationType.ADD, "depth" : .9 * mm, "offsetDistance" : 25.4 * mm});
        }
        {
            var Q0;
            {var subQ0=sQuery(id+"F5.wireOp",EDGE,"E20.left");Q0=makeQuery(id+"F14.boolean.opBoolean","MERGE",FACE,{"derivedFrom":[makeQuery(id+"F7.boolean.opBoolean","MERGE",FACE,{"derivedFrom":[makeQuery(id+"F6.opExtrude","SWEPT_FACE",FACE,{"disambiguationData":[OSD([sQuery(id+"F5.wireOp",EDGE,"E15.left"),sQuery(id+"F5.wireOp",EDGE,"E17.left"),sQuery(id+"F5.wireOp",EDGE,"E19.left"),subQ0])]}),makeQuery(id+"F7.opExtrude","SWEPT_FACE",FACE,{"disambiguationData":[OSD([subQ0])]})]}),makeQuery(id+"F14.opExtrude","SWEPT_FACE",FACE,{"disambiguationData":[OSD([sQuery(id+"F12.wireOp",EDGE,"E25.left")])]})]});}
            var sketch = newSketch(context, id + "F22", { "sketchPlane" : qUnion([Q0])});
            skLineSegment(sketch, "E32.bottom", {"start": v(0.65, 1.8) * mm, "end": v(-0.85, 1.8) * mm});
            skLineSegment(sketch, "E32.top", {"start": v(0.65, 6.3) * mm, "end": v(-0.85, 6.3) * mm});
            skLineSegment(sketch, "E32.left", {"start": v(0.65, 1.8) * mm, "end": v(0.65, 6.3) * mm});
            skLineSegment(sketch, "E32.right", {"start": v(-0.85, 1.8) * mm, "end": v(-0.85, 6.3) * mm});
            skSolve(sketch);
        }
        {
            var Q0;
            Q0=makeQuery(id+"F22.imprint","IMPRINT",FACE,{"disambiguationData":[TD([[makeQuery(id+"F22.imprint","IMPRINT",EDGE,{"derivedFrom":sQuery(id+"F22.wireOp",EDGE,"E32.bottom")}),1.0]])]});
            extrude(context, id + "F23", {"entities" : qUnion([Q0]), "operationType" : NewBodyOperationType.ADD, "depth" : .9 * mm, "offsetDistance" : 25.4 * mm});
        }
        {
            var Q0;
            Q0=makeQuery(id+"F23.opExtrude","CAP_EDGE",EDGE,{"disambiguationData":[OSD([sQuery(id+"F22.wireOp",EDGE,"E32.left")])],"isStart":false});
            var Q1;
            Q1=makeQuery(id+"F21.opExtrude","CAP_EDGE",EDGE,{"disambiguationData":[OSD([sQuery(id+"F20.wireOp",EDGE,"E31.left")])],"isStart":false});
            chamfer(context, id + "F24", {"entities" : qUnion([Q0, Q1]), "width" : .9 * mm, "tangentPropagation" : true});
        }
        {
            var Q0;
            {var subQ0=sQuery(id+"F22.wireOp",EDGE,"E32.left");Q0=makeQuery(id+"F24.opChamfer","BLEND_EDGE",EDGE,{"blendedFrom":[makeQuery(id+"F23.opExtrude","CAP_EDGE",EDGE,{"disambiguationData":[OSD([subQ0])],"isStart":false}),makeQuery(id+"F23.opExtrude","CAP_FACE",FACE,{"disambiguationData":[OSD([sQuery(id+"F22.wireOp",EDGE,"E32.bottom"),sQuery(id+"F22.wireOp",EDGE,"E32.top"),subQ0,sQuery(id+"F22.wireOp",EDGE,"E32.right")])],"isStart":false})],"blendedInto":[makeQuery(id+"F23.opExtrude","CAP_FACE",FACE,{"disambiguationData":[OSD([sQuery(id+"F22.wireOp",EDGE,"E32.bottom"),sQuery(id+"F22.wireOp",EDGE,"E32.top"),subQ0,sQuery(id+"F22.wireOp",EDGE,"E32.right")])],"isStart":false})]});}
            var Q1;
            Q1=makeQuery(id+"F23.opExtrude","CAP_EDGE",EDGE,{"disambiguationData":[OSD([sQuery(id+"F22.wireOp",EDGE,"E32.right")])],"isStart":false});
            var Q2;
            {var subQ0=sQuery(id+"F20.wireOp",EDGE,"E31.left");Q2=makeQuery(id+"F24.opChamfer","BLEND_EDGE",EDGE,{"blendedFrom":[makeQuery(id+"F21.opExtrude","CAP_EDGE",EDGE,{"disambiguationData":[OSD([subQ0])],"isStart":false}),makeQuery(id+"F21.opExtrude","CAP_FACE",FACE,{"disambiguationData":[OSD([sQuery(id+"F20.wireOp",EDGE,"E31.bottom"),sQuery(id+"F20.wireOp",EDGE,"E31.top"),subQ0,sQuery(id+"F20.wireOp",EDGE,"E31.right")])],"isStart":false})],"blendedInto":[makeQuery(id+"F21.opExtrude","CAP_FACE",FACE,{"disambiguationData":[OSD([sQuery(id+"F20.wireOp",EDGE,"E31.bottom"),sQuery(id+"F20.wireOp",EDGE,"E31.top"),subQ0,sQuery(id+"F20.wireOp",EDGE,"E31.right")])],"isStart":false})]});}
            var Q3;
            Q3=makeQuery(id+"F21.opExtrude","CAP_EDGE",EDGE,{"disambiguationData":[OSD([sQuery(id+"F20.wireOp",EDGE,"E31.right")])],"isStart":false});
            fillet(context, id + "F25", {"entities" : qUnion([Q0, Q1, Q2, Q3]), "radius" : .5 * mm, "tangentPropagation" : true, "allowEdgeOverflow" : false});
        }
    });
